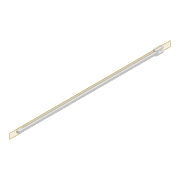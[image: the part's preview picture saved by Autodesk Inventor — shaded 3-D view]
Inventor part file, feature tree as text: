
AUTODESK INVENTOR PART (.ipt)
format: ipt  version: 2022 (Build 260153000, 153)  size: 158,208 bytes
history: native  units: mm
features: extrude x6, sketch x5, projected_geometry x4
ambient origin geometry x8: Origin, YZ Plane, XZ Plane, XY Plane, X Axis, Y Axis, Z Axis, Center Point
bodies: Solid1 (feature_tree)
feature tree (15):
  extrude  "Extrusion1"  Depth=10.0mm
  sketch  "Sketch2"  dims[d3=399.562mm d6=6.0mm d7=0.0mm]
  extrude  "Extrusion2"  Depth=6.0mm TaperAngle=0.0deg
  extrude  "Extrusion3"  Depth=3.3mm
  extrude  "Extrusion4"  Depth=10.0mm
  extrude  "Extrusion5"  Depth=4.0mm TaperAngle=0.0deg
  extrude  "Extrusion6"  Depth=10.0mm
  sketch  "Sketch1"  dims[d1=3.3mm d2=10.0mm]
  projected_geometry  "Projected Loop1"
  sketch  "Sketch3"  dims[d16=3.3mm d17=20.0mm]
  projected_geometry  "Projected Loop2"
  sketch  "Sketch4"  dims[d18=10.0mm d20=15.0mm]
  projected_geometry  "Projected Loop3"
  sketch  "Sketch5"  dims[d21=10.0mm d22=4.0mm d23=0.0mm d24=10.0mm d25=15.0mm d26=4.0mm d27=0.0mm d28=6.0mm d29=0.0mm d30=0.2mm d31=0.0mm d32=0.2mm d33=0.0mm]
  projected_geometry  "Projected Loop4"
